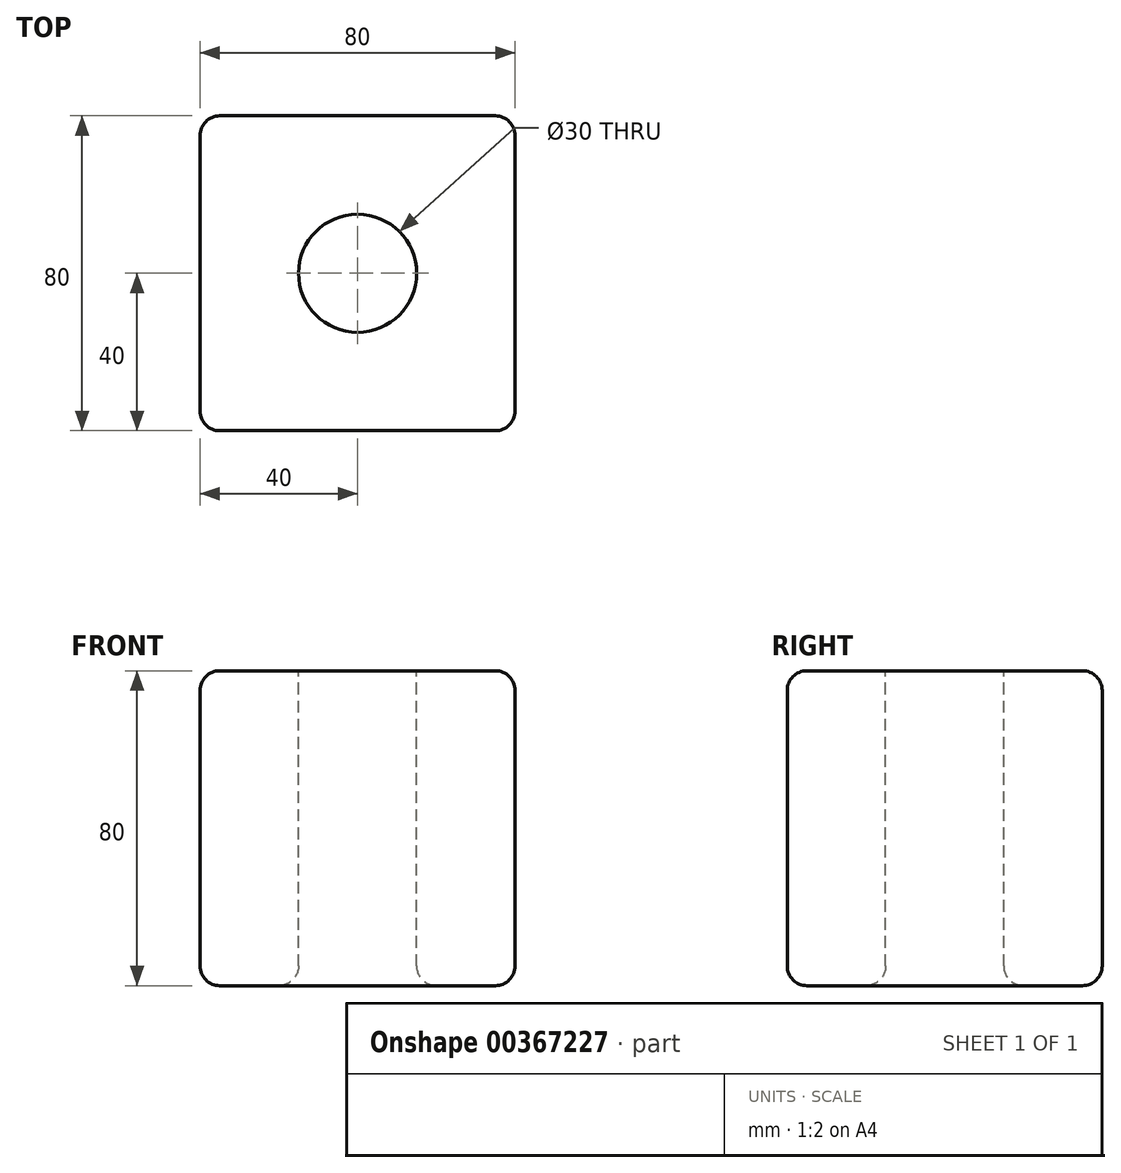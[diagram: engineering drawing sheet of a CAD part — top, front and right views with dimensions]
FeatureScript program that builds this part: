
annotation { "Feature Type Name" : "Feature", "Feature Type Description" : "" }
export const myFeature = defineFeature(function(context is Context, id is Id, definition is map)
    precondition{}
    {
        {
            var Q0;
            Q0=qCreatedBy(makeId("Top.planeOp"),FACE);
            var sketch = newSketch(context, id + "F0", { "sketchPlane" : qUnion([Q0])});
            skLineSegment(sketch, "E0.bottom", {"start": v(-40, 40) * mm, "end": v(40, 40) * mm});
            skLineSegment(sketch, "E0.top", {"start": v(-40, -40) * mm, "end": v(40, -40) * mm});
            skLineSegment(sketch, "E0.left", {"start": v(-40, 40) * mm, "end": v(-40, -40) * mm});
            skLineSegment(sketch, "E0.right", {"start": v(40, 40) * mm, "end": v(40, -40) * mm});
            skPoint(sketch, "E0.middle", {"position": v(0, 0) * mm});
            skSolve(sketch);
        }
        {
            var Q0;
            Q0=makeQuery(id+"F0.imprint","IMPRINT",FACE,{"disambiguationData":[TD([[makeQuery(id+"F0.imprint","IMPRINT",EDGE,{"derivedFrom":sQuery(id+"F0.wireOp",EDGE,"E0.bottom")}),-1.0]])]});
            extrude(context, id + "F1", {"entities" : qUnion([Q0]), "depth" : 80 * mm});
        }
        {
            var Q0;
            Q0=makeQuery(id+"F1.opExtrude","CAP_FACE",FACE,{"disambiguationData":[OSD([sQuery(id+"F0.wireOp",EDGE,"E0.bottom"),sQuery(id+"F0.wireOp",EDGE,"E0.top"),sQuery(id+"F0.wireOp",EDGE,"E0.left"),sQuery(id+"F0.wireOp",EDGE,"E0.right")])],"isStart":false});
            var sketch = newSketch(context, id + "F2", { "sketchPlane" : qUnion([Q0])});
            skCircle(sketch, "E1", {"center": v(0, 0) * mm, "radius": 15 * mm});
            skSolve(sketch);
        }
        {
            var Q0;
            Q0=makeQuery(id+"F2.imprint","IMPRINT",FACE,{"disambiguationData":[TD([[makeQuery(id+"F2.imprint","IMPRINT",EDGE,{"derivedFrom":sQuery(id+"F2.wireOp",EDGE,"E1")}),1.0]])]});
            extrude(context, id + "F3", {"entities" : qUnion([Q0]), "operationType" : NewBodyOperationType.REMOVE, "endBound" : BoundingType.THROUGH_ALL, "oppositeDirection" : true, "depth" : 25 * mm});
        }
        {
            var Q0;
            Q0=makeQuery(id+"F1.opExtrude","SWEPT_EDGE",EDGE,{"disambiguationData":[OSD([sQuery(id+"F0.wireOp",EDGE,"E0.bottom"),sQuery(id+"F0.wireOp",EDGE,"E0.right")])]});
            var Q1;
            Q1=makeQuery(id+"F1.opExtrude","CAP_EDGE",EDGE,{"disambiguationData":[OSD([sQuery(id+"F0.wireOp",EDGE,"E0.right")])],"isStart":true});
            var Q2;
            Q2=makeQuery(id+"F1.opExtrude","SWEPT_EDGE",EDGE,{"disambiguationData":[OSD([sQuery(id+"F0.wireOp",EDGE,"E0.top"),sQuery(id+"F0.wireOp",EDGE,"E0.right")])]});
            var Q3;
            Q3=makeQuery(id+"F1.opExtrude","CAP_EDGE",EDGE,{"disambiguationData":[OSD([sQuery(id+"F0.wireOp",EDGE,"E0.top")])],"isStart":false});
            var Q4;
            Q4=makeQuery(id+"F1.opExtrude","CAP_EDGE",EDGE,{"disambiguationData":[OSD([sQuery(id+"F0.wireOp",EDGE,"E0.right")])],"isStart":false});
            var Q5;
            Q5=makeQuery(id+"F1.opExtrude","CAP_EDGE",EDGE,{"disambiguationData":[OSD([sQuery(id+"F0.wireOp",EDGE,"E0.bottom")])],"isStart":false});
            var Q6;
            Q6=makeQuery(id+"F1.opExtrude","CAP_EDGE",EDGE,{"disambiguationData":[OSD([sQuery(id+"F0.wireOp",EDGE,"E0.bottom")])],"isStart":true});
            var Q7;
            Q7=makeQuery(id+"F1.opExtrude","SWEPT_EDGE",EDGE,{"disambiguationData":[OSD([sQuery(id+"F0.wireOp",EDGE,"E0.bottom"),sQuery(id+"F0.wireOp",EDGE,"E0.left")])]});
            var Q8;
            Q8=makeQuery(id+"F1.opExtrude","CAP_EDGE",EDGE,{"disambiguationData":[OSD([sQuery(id+"F0.wireOp",EDGE,"E0.left")])],"isStart":true});
            var Q9;
            Q9=makeQuery(id+"F1.opExtrude","CAP_EDGE",EDGE,{"disambiguationData":[OSD([sQuery(id+"F0.wireOp",EDGE,"E0.top")])],"isStart":true});
            var Q10;
            Q10=makeQuery(id+"F1.opExtrude","SWEPT_EDGE",EDGE,{"disambiguationData":[OSD([sQuery(id+"F0.wireOp",EDGE,"E0.top"),sQuery(id+"F0.wireOp",EDGE,"E0.left")])]});
            var Q11;
            Q11=makeQuery(id+"F1.opExtrude","CAP_EDGE",EDGE,{"disambiguationData":[OSD([sQuery(id+"F0.wireOp",EDGE,"E0.left")])],"isStart":false});
            var Q12;
            Q12=makeQuery(id+"F3.boolean.opBoolean","COPY",EDGE,{"derivedFrom":makeQuery(id+"F3.opExtrude","CAP_EDGE",EDGE,{"disambiguationData":[OSD([sQuery(id+"F2.wireOp",EDGE,"E1")])],"isStart":true})});
            var Q13;
            Q13=makeQuery(id+"F3.boolean.opBoolean","INTERSECT",EDGE,{"derivedFrom":[makeQuery(id+"F1.opExtrude","CAP_FACE",FACE,{"disambiguationData":[OSD([sQuery(id+"F0.wireOp",EDGE,"E0.bottom"),sQuery(id+"F0.wireOp",EDGE,"E0.top"),sQuery(id+"F0.wireOp",EDGE,"E0.left"),sQuery(id+"F0.wireOp",EDGE,"E0.right")])],"isStart":true}),makeQuery(id+"F3.opExtrude","SWEPT_FACE",FACE,{"disambiguationData":[OSD([sQuery(id+"F2.wireOp",EDGE,"E1")])]})]});
            fillet(context, id + "F4", {"entities" : qUnion([Q0, Q1, Q2, Q3, Q4, Q5, Q6, Q7, Q8, Q9, Q10, Q11, Q12, Q13]), "radius" : 5 * mm, "tangentPropagation" : true, "allowEdgeOverflow" : false});
        }
    });
